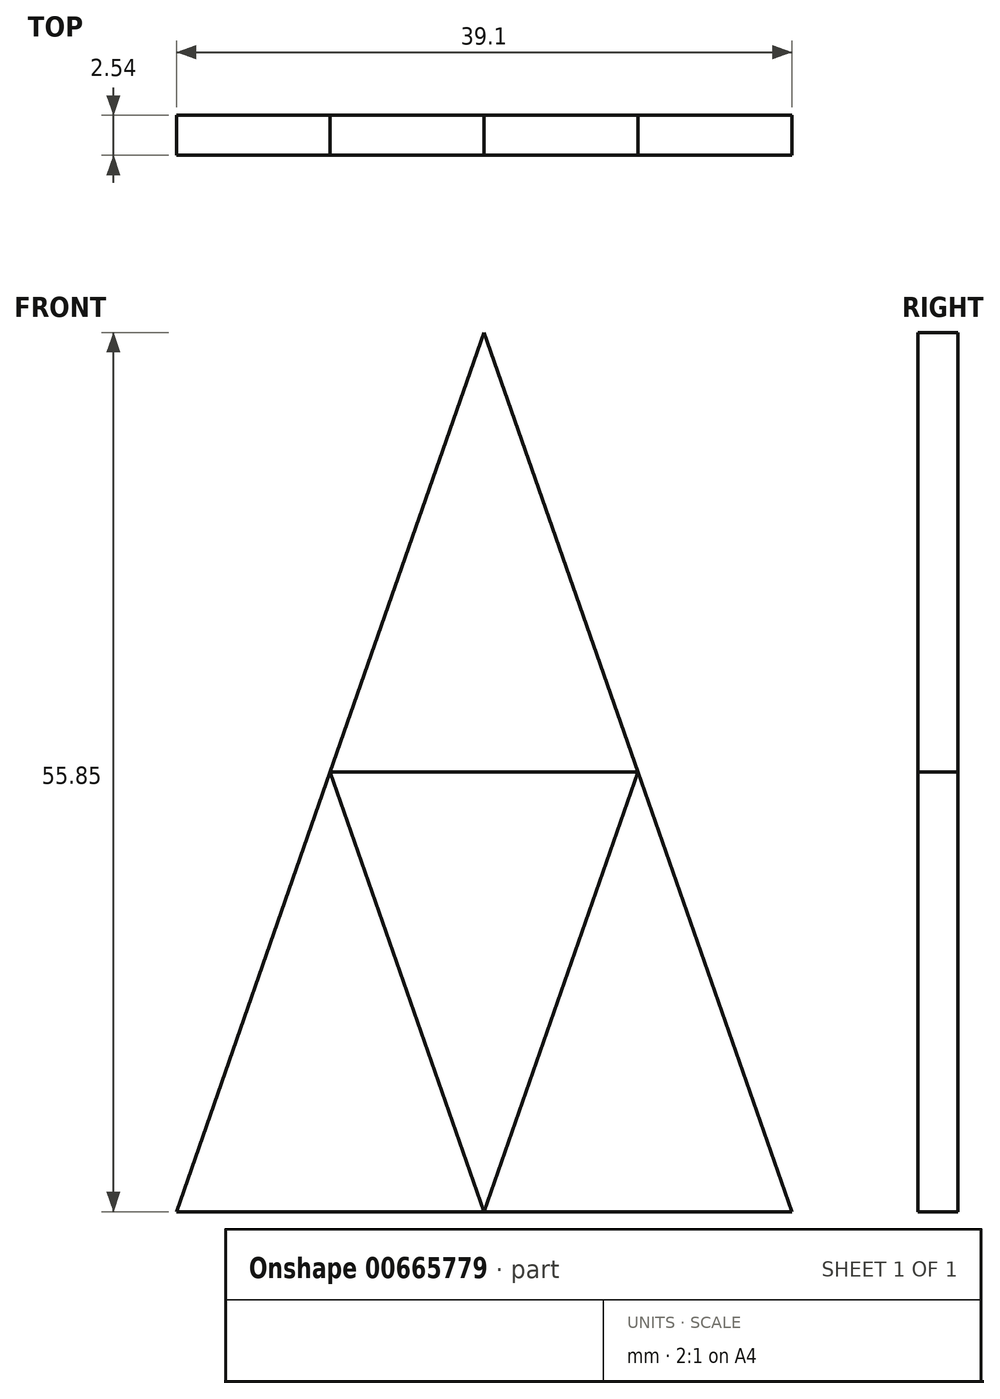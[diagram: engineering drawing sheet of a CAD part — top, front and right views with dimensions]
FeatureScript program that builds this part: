
annotation { "Feature Type Name" : "Feature", "Feature Type Description" : "" }
export const myFeature = defineFeature(function(context is Context, id is Id, definition is map)
    precondition{}
    {
        {
            var Q0;
            Q0=qCreatedBy(makeId("Front.planeOp"),FACE);
            var sketch = newSketch(context, id + "F0", { "sketchPlane" : qUnion([Q0])});
            skLineSegment(sketch, "E0", {"start": v(-42.62, -55.85) * mm, "end": v(-3.52, -55.85) * mm});
            skLineSegment(sketch, "E1", {"start": v(-23.07, 0) * mm, "end": v(-3.52, -55.85) * mm});
            skPoint(sketch, "E1.startSnap0", {"position": v(-23.07, -55.85) * mm});
            skLineSegment(sketch, "E2", {"start": v(-23.07, 0) * mm, "end": v(-42.62, -55.85) * mm});
            skLineSegment(sketch, "E3", {"start": v(-32.84, -27.92) * mm, "end": v(-23.07, -55.85) * mm});
            skLineSegment(sketch, "E4", {"start": v(-23.07, -55.85) * mm, "end": v(-13.3, -27.92) * mm});
            skLineSegment(sketch, "E5", {"start": v(-13.3, -27.92) * mm, "end": v(-32.84, -27.92) * mm});
            skSolve(sketch);
        }
        {
            var Q0;
            {var subQ3=sQuery(id+"F0.wireOp",EDGE,"E5");Q0=makeQuery(id+"F0.imprint","IMPRINT",FACE,{"disambiguationData":[TD([[makeQuery(id+"F0.imprint","IMPRINT",EDGE,{"derivedFrom":subQ3}),-1.0]])]});}
            var Q1;
            {var subQ3=sQuery(id+"F0.wireOp",EDGE,"E3");Q1=makeQuery(id+"F0.imprint","IMPRINT",FACE,{"disambiguationData":[TD([[makeQuery(id+"F0.imprint","IMPRINT",EDGE,{"derivedFrom":subQ3}),-1.0]])]});}
            var Q2;
            {var subQ3=sQuery(id+"F0.wireOp",EDGE,"E4");Q2=makeQuery(id+"F0.imprint","IMPRINT",FACE,{"disambiguationData":[TD([[makeQuery(id+"F0.imprint","IMPRINT",EDGE,{"derivedFrom":subQ3}),-1.0]])]});}
            extrude(context, id + "F1", {"entities" : qUnion([Q0, Q1, Q2]), "depth" : 2.54 * mm, "offsetDistance" : 25.4 * mm});
        }
        {
            var Q0;
            Q0=makeQuery(id+"F0.imprint","IMPRINT",FACE,{"disambiguationData":[TD([[makeQuery(id+"F0.imprint","IMPRINT",EDGE,{"derivedFrom":sQuery(id+"F0.wireOp",EDGE,"E3")}),1.0]])]});
            extrude(context, id + "F2", {"entities" : qUnion([Q0]), "depth" : 2.54 * mm, "offsetDistance" : 25.4 * mm});
        }
    });
